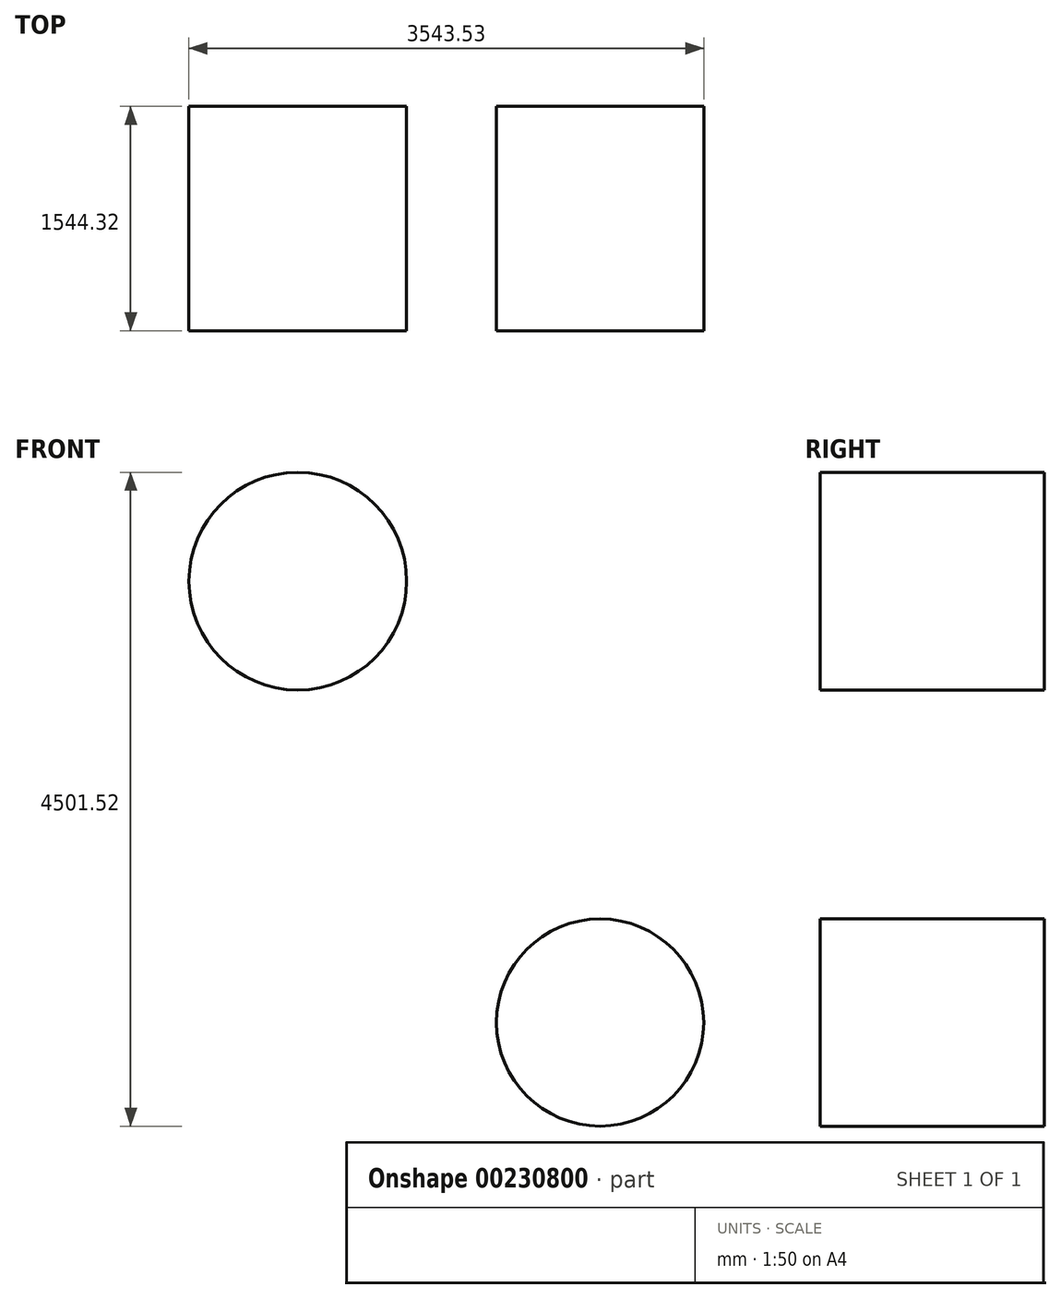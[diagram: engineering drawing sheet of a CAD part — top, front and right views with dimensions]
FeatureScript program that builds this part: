
annotation { "Feature Type Name" : "Feature", "Feature Type Description" : "" }
export const myFeature = defineFeature(function(context is Context, id is Id, definition is map)
    precondition{}
    {
        {
            var Q0;
            Q0=qCreatedBy(makeId("Front.planeOp"),FACE);
            var sketch = newSketch(context, id + "F0", { "sketchPlane" : qUnion([Q0])});
            skCircle(sketch, "E0", {"center": v(-1036.34, 1506.04) * mm, "radius": 749.3 * mm});
            skCircle(sketch, "E1", {"center": v(1044.67, -1532.96) * mm, "radius": 713.22 * mm});
            skSolve(sketch);
        }
        {
            var Q0;
            Q0=makeQuery(id+"F0.imprint","IMPRINT",FACE,{"disambiguationData":[TD([[makeQuery(id+"F0.imprint","IMPRINT",EDGE,{"derivedFrom":sQuery(id+"F0.wireOp",EDGE,"E0")}),1.0]])]});
            var Q1;
            Q1=makeQuery(id+"F0.imprint","IMPRINT",FACE,{"disambiguationData":[TD([[makeQuery(id+"F0.imprint","IMPRINT",EDGE,{"derivedFrom":sQuery(id+"F0.wireOp",EDGE,"E1")}),1.0]])]});
            extrude(context, id + "F1", {"entities" : qUnion([Q0, Q1]), "depth" : 1544.32 * mm});
        }
    });
